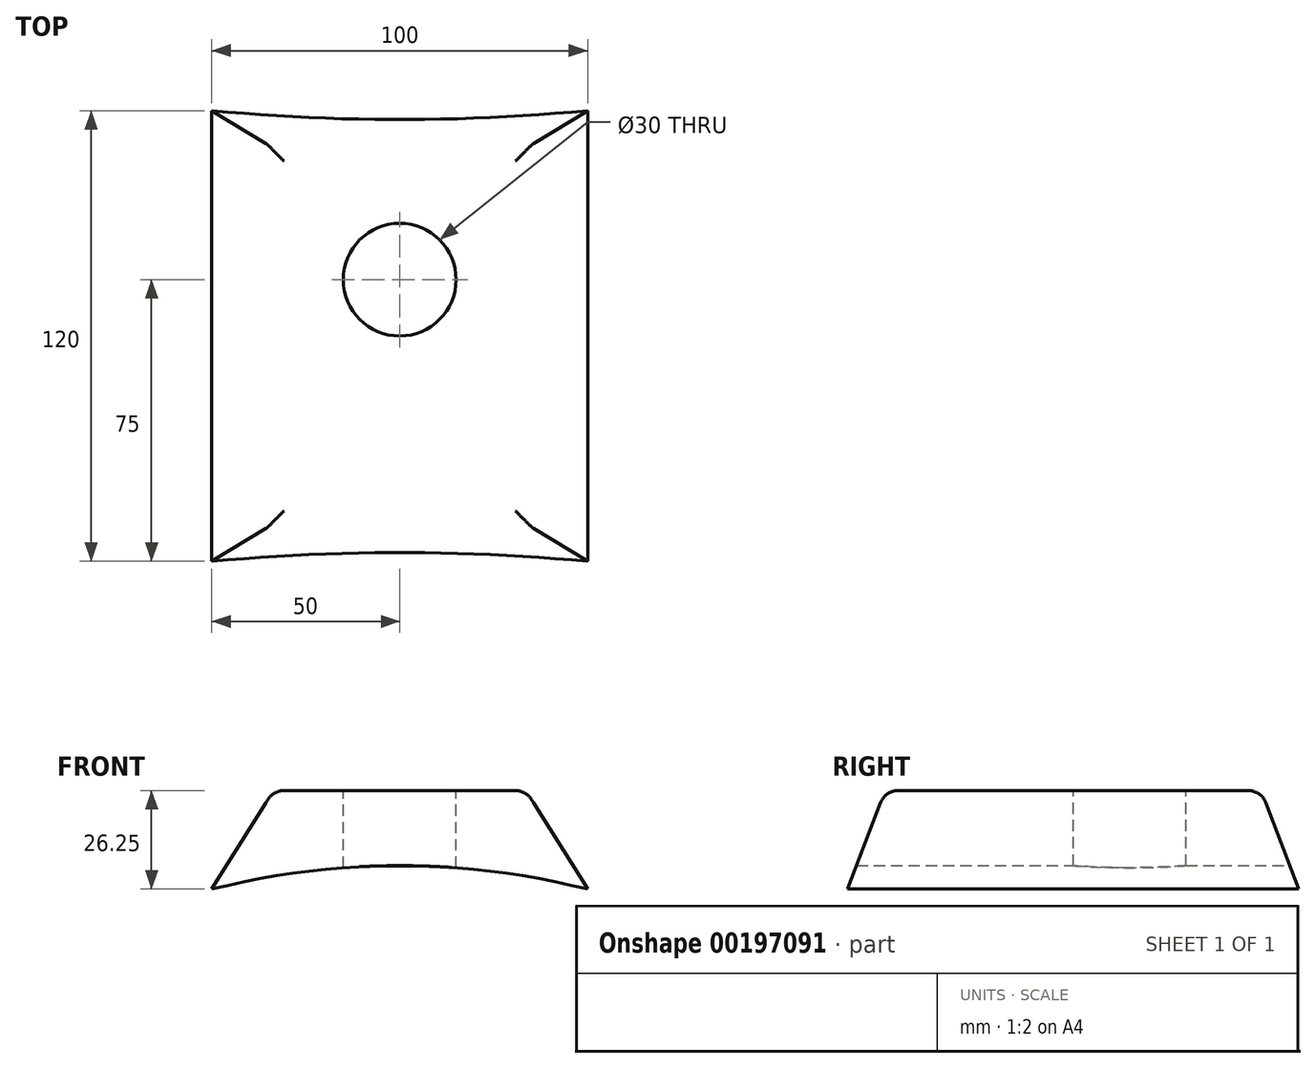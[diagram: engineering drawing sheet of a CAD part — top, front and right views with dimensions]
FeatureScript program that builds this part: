
annotation { "Feature Type Name" : "Feature", "Feature Type Description" : "" }
export const myFeature = defineFeature(function(context is Context, id is Id, definition is map)
    precondition{}
    {
        {
            var Q0;
            Q0=qCreatedBy(makeId("Front.planeOp"),FACE);
            var sketch = newSketch(context, id + "F0", { "sketchPlane" : qUnion([Q0])});
            skArc(sketch, "E0", {"start": v(50, 196.95) * mm, "mid": v(0, 203.2) * mm, "end": v(-50, 196.95) * mm});
            skLineSegment(sketch, "E1", {"start": v(-30.76, 223.2) * mm, "end": v(30.76, 223.2) * mm});
            skLineSegment(sketch, "E2", {"start": v(0, 0) * mm, "end": v(0, 303.23) * mm, "construction": true});
            skLineSegment(sketch, "E3", {"start": v(-50, 196.95) * mm, "end": v(-35, 220.86) * mm});
            skArc(sketch, "E4.filletArc", {"start": v(-30.76, 223.2) * mm, "mid": v(-33.18, 222.58) * mm, "end": v(-35, 220.86) * mm});
            skArc(sketch, "E5.MirrorCS", {"start": v(30.76, 223.2) * mm, "mid": v(33.18, 222.58) * mm, "end": v(35, 220.86) * mm});
            skLineSegment(sketch, "E6.MirrorCS", {"start": v(50, 196.95) * mm, "end": v(35, 220.86) * mm});
            skSolve(sketch);
        }
        {
            var Q0;
            Q0=makeQuery(id+"F0.imprint","IMPRINT",FACE,{"disambiguationData":[TD([[makeQuery(id+"F0.imprint","IMPRINT",EDGE,{"derivedFrom":sQuery(id+"F0.wireOp",EDGE,"E0")}),-1.0]])]});
            extrude(context, id + "F1", {"entities" : qUnion([Q0]), "endBound" : BoundingType.SYMMETRIC, "depth" : 120 * mm});
        }
        {
            var Q0;
            Q0=qCreatedBy(makeId("Right.planeOp"),FACE);
            var sketch = newSketch(context, id + "F2", { "sketchPlane" : qUnion([Q0])});
            skLineSegment(sketch, "E7.0", {"start": v(-46.55, 223.2) * mm, "end": v(46.55, 223.2) * mm});
            skLineSegment(sketch, "E8", {"start": v(-60, 196.95) * mm, "end": v(-51.23, 219.98) * mm});
            skLineSegment(sketch, "E9", {"start": v(60, 196.95) * mm, "end": v(51.23, 219.98) * mm});
            skPoint(sketch, "E10.newPointA", {"position": v(-50, 223.2) * mm});
            skPoint(sketch, "E10.newPointB", {"position": v(-60, 223.2) * mm});
            skArc(sketch, "E10.filletArc", {"start": v(-46.55, 223.2) * mm, "mid": v(-49.4, 222.32) * mm, "end": v(-51.23, 219.98) * mm});
            skPoint(sketch, "E11.newPointA", {"position": v(50, 223.2) * mm});
            skPoint(sketch, "E11.newPointB", {"position": v(60, 223.2) * mm});
            skArc(sketch, "E11.filletArc", {"start": v(51.23, 219.98) * mm, "mid": v(49.4, 222.32) * mm, "end": v(46.55, 223.2) * mm});
            skLineSegment(sketch, "E12", {"start": v(-60, 223.2) * mm, "end": v(-46.55, 223.2) * mm});
            skLineSegment(sketch, "E13", {"start": v(46.55, 223.2) * mm, "end": v(60, 223.2) * mm});
            skLineSegment(sketch, "E14", {"start": v(-60, 223.2) * mm, "end": v(-60, 196.95) * mm});
            skLineSegment(sketch, "E15", {"start": v(60, 223.2) * mm, "end": v(60, 196.95) * mm});
            skSolve(sketch);
        }
        {
            var Q0;
            Q0 = qSketchRegion(id + "F2", true);
            extrude(context, id + "F3", {"entities" : qUnion([Q0]), "operationType" : NewBodyOperationType.REMOVE, "endBound" : BoundingType.SYMMETRIC, "depth" : 150 * mm});
        }
        {
            var Q0;
            Q0=makeQuery(id+"F1.opExtrude","SWEPT_FACE",FACE,{"disambiguationData":[OSD([sQuery(id+"F0.wireOp",EDGE,"E1")])]});
            var sketch = newSketch(context, id + "F4", { "sketchPlane" : qUnion([Q0])});
            skCircle(sketch, "E16", {"center": v(0, 15) * mm, "radius": 15 * mm});
            skSolve(sketch);
        }
        {
            var Q0;
            Q0=makeQuery(id+"F4.imprint","IMPRINT",FACE,{"disambiguationData":[TD([[makeQuery(id+"F4.imprint","IMPRINT",EDGE,{"derivedFrom":sQuery(id+"F4.wireOp",EDGE,"AqqI3Bb0-dFgM-uRxO-t4WF-vuwFte1x1O8o")}),1.0]])]});
            var Q1;
            Q1=makeQuery(id+"F4.imprint","IMPRINT",FACE,{"disambiguationData":[TD([[makeQuery(id+"F4.imprint","IMPRINT",EDGE,{"derivedFrom":sQuery(id+"F4.wireOp",EDGE,"E16")}),1.0]])]});
            extrude(context, id + "F5", {"entities" : qUnion([Q0, Q1]), "operationType" : NewBodyOperationType.REMOVE, "oppositeDirection" : true, "depth" : 25 * mm});
        }
    });
